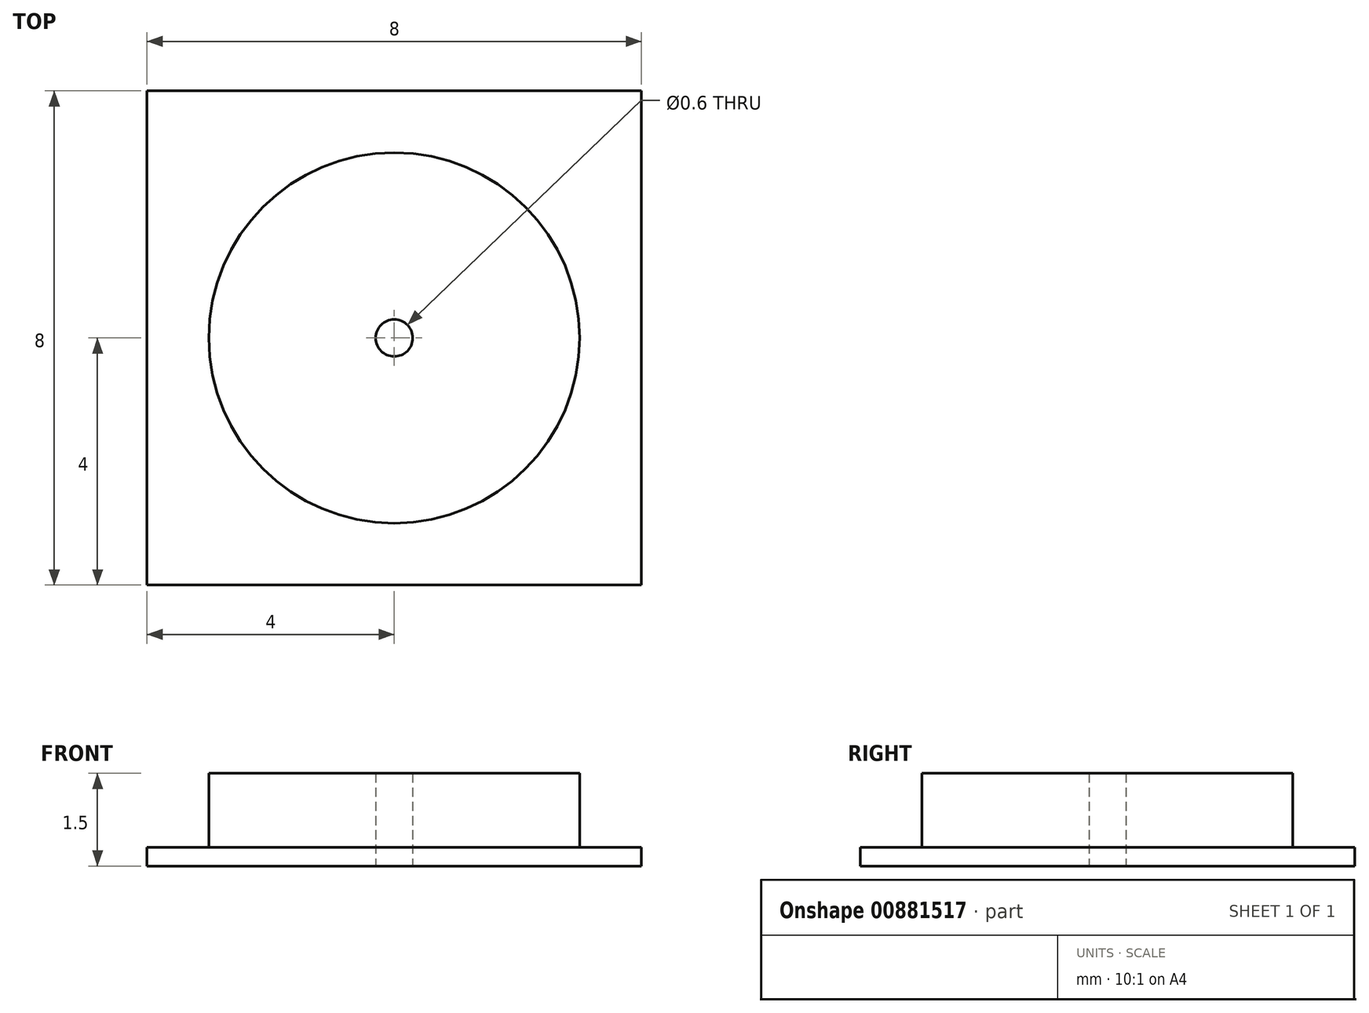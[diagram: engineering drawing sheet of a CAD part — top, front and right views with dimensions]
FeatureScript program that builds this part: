
annotation { "Feature Type Name" : "Feature", "Feature Type Description" : "" }
export const myFeature = defineFeature(function(context is Context, id is Id, definition is map)
    precondition{}
    {
        {
            var Q0;
            Q0=qCreatedBy(makeId("Top.planeOp"),FACE);
            var sketch = newSketch(context, id + "F0", { "sketchPlane" : qUnion([Q0])});
            skLineSegment(sketch, "E0.bottom", {"start": v(4, -4) * mm, "end": v(-4, -4) * mm});
            skLineSegment(sketch, "E0.top", {"start": v(4, 4) * mm, "end": v(-4, 4) * mm});
            skLineSegment(sketch, "E0.left", {"start": v(4, -4) * mm, "end": v(4, 4) * mm});
            skLineSegment(sketch, "E0.right", {"start": v(-4, -4) * mm, "end": v(-4, 4) * mm});
            skPoint(sketch, "E0.middle", {"position": v(0, 0) * mm});
            skCircle(sketch, "E1", {"center": v(0, 0) * mm, "radius": 0.3 * mm});
            skSolve(sketch);
        }
        {
            var Q0;
            Q0=makeQuery(id+"F0.imprint","IMPRINT",FACE,{"disambiguationData":[TD([[makeQuery(id+"F0.imprint","IMPRINT",EDGE,{"derivedFrom":sQuery(id+"F0.wireOp",EDGE,"E0.bottom")}),-1.0]])]});
            extrude(context, id + "F1", {"entities" : qUnion([Q0]), "depth" : 0.3 * mm, "offsetDistance" : 25 * mm});
        }
        {
            var Q0;
            Q0=makeQuery(id+"F1.opExtrude","CAP_FACE",FACE,{"disambiguationData":[OSD([sQuery(id+"F0.wireOp",EDGE,"E0.bottom"),sQuery(id+"F0.wireOp",EDGE,"E0.top"),sQuery(id+"F0.wireOp",EDGE,"E0.left"),sQuery(id+"F0.wireOp",EDGE,"E0.right"),sQuery(id+"F0.wireOp",EDGE,"E1")])],"isStart":false});
            var sketch = newSketch(context, id + "F2", { "sketchPlane" : qUnion([Q0])});
            skCircle(sketch, "E2", {"center": v(0, 0) * mm, "radius": 3 * mm});
            skSolve(sketch);
        }
        {
            var Q0;
            Q0=makeQuery(id+"F2.imprint","IMPRINT",FACE,{"disambiguationData":[TD([[makeQuery(id+"F2.imprint","IMPRINT",EDGE,{"derivedFrom":sQuery(id+"F2.wireOp",EDGE,"E2")}),1.0]])]});
            extrude(context, id + "F3", {"entities" : qUnion([Q0]), "operationType" : NewBodyOperationType.ADD, "depth" : 1.2 * mm, "offsetDistance" : 25 * mm});
        }
    });
